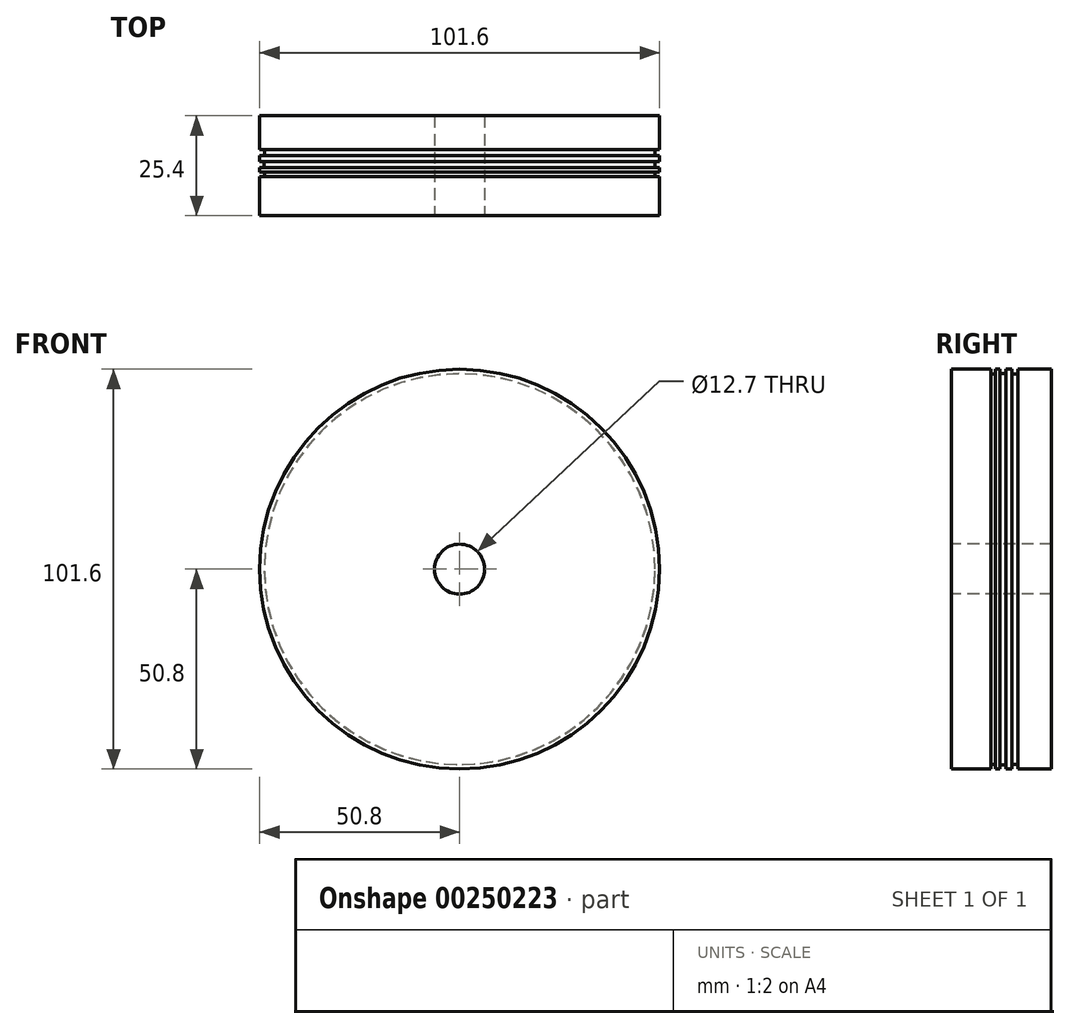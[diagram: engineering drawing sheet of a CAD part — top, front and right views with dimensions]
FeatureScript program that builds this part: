
annotation { "Feature Type Name" : "Feature", "Feature Type Description" : "" }
export const myFeature = defineFeature(function(context is Context, id is Id, definition is map)
    precondition{}
    {
        {
            var Q0;
            Q0=qCreatedBy(makeId("Top.planeOp"),FACE);
            var sketch = newSketch(context, id + "F0", { "sketchPlane" : qUnion([Q0])});
            skLineSegment(sketch, "E0", {"start": v(0, 0) * mm, "end": v(0, 25.4) * mm});
            skLineSegment(sketch, "E1", {"start": v(0, 0) * mm, "end": v(-6.35, 0) * mm});
            skLineSegment(sketch, "E2", {"start": v(-6.35, 0) * mm, "end": v(-6.35, 25.4) * mm});
            skLineSegment(sketch, "E3", {"start": v(-50.8, 0) * mm, "end": v(-6.35, 0) * mm});
            skLineSegment(sketch, "E4", {"start": v(-50.8, 0) * mm, "end": v(-50.8, 34.6) * mm});
            skLineSegment(sketch, "E5", {"start": v(-6.35, 25.4) * mm, "end": v(-50.8, 25.4) * mm});
            skLineSegment(sketch, "E6", {"start": v(-50.8, 9.91) * mm, "end": v(-49.62, 9.91) * mm});
            skLineSegment(sketch, "E7", {"start": v(-49.62, 9.91) * mm, "end": v(-49.62, 11.06) * mm});
            skLineSegment(sketch, "E8", {"start": v(-49.62, 11.06) * mm, "end": v(-50.8, 11.06) * mm});
            skLineSegment(sketch, "E9", {"start": v(-50.8, 11.06) * mm, "end": v(-50.8, 12.2) * mm});
            skLineSegment(sketch, "E10", {"start": v(-50.8, 12.2) * mm, "end": v(-49.67, 12.2) * mm});
            skLineSegment(sketch, "E11", {"start": v(-49.67, 12.2) * mm, "end": v(-49.67, 13.73) * mm});
            skLineSegment(sketch, "E12", {"start": v(-49.67, 13.73) * mm, "end": v(-50.8, 13.73) * mm});
            skLineSegment(sketch, "E13", {"start": v(-50.8, 13.73) * mm, "end": v(-50.8, 15.26) * mm});
            skLineSegment(sketch, "E14", {"start": v(-50.8, 15.26) * mm, "end": v(-49.61, 15.26) * mm});
            skLineSegment(sketch, "E15", {"start": v(-49.61, 15.26) * mm, "end": v(-49.61, 16.8) * mm});
            skLineSegment(sketch, "E16", {"start": v(-49.61, 16.8) * mm, "end": v(-50.8, 16.8) * mm});
            skSolve(sketch);
        }
        {
            var Q0;
            Q0=makeQuery(id+"F0.imprint","IMPRINT",FACE,{"disambiguationData":[TD([[makeQuery(id+"F0.imprint","IMPRINT",EDGE,{"derivedFrom":sQuery(id+"F0.wireOp",EDGE,"E2")}),1.0]])]});
            var Q1;
            Q1=sQuery(id+"F0.wireOp",EDGE,"E0");
            revolve(context, id + "F1", {"entities" : qUnion([Q0]), "axis" : qUnion([Q1]), "revolveType" : RevolveType.FULL});
        }
    });
